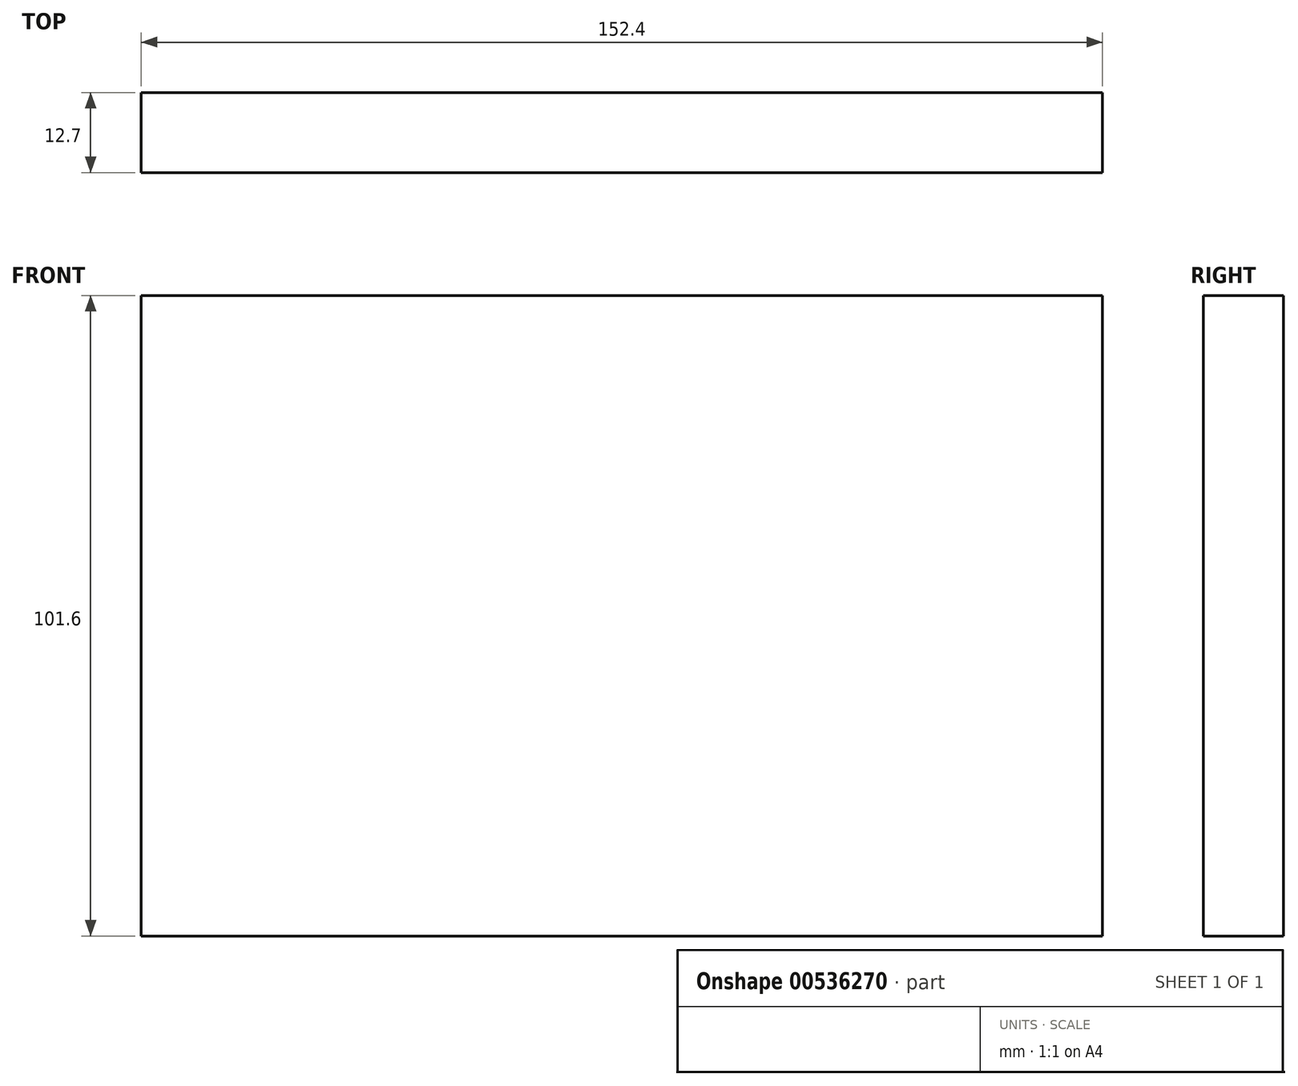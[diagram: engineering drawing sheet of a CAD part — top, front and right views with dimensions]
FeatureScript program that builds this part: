
annotation { "Feature Type Name" : "Feature", "Feature Type Description" : "" }
export const myFeature = defineFeature(function(context is Context, id is Id, definition is map)
    precondition{}
    {
        {
            var Q0;
            Q0=qCreatedBy(makeId("Front.planeOp"),FACE);
            var sketch = newSketch(context, id + "F0", { "sketchPlane" : qUnion([Q0])});
            skLineSegment(sketch, "E0.bottom", {"start": v(-76.2, 50.8) * mm, "end": v(76.2, 50.8) * mm});
            skLineSegment(sketch, "E0.top", {"start": v(-76.2, -50.8) * mm, "end": v(76.2, -50.8) * mm});
            skLineSegment(sketch, "E0.left", {"start": v(-76.2, 50.8) * mm, "end": v(-76.2, -50.8) * mm});
            skLineSegment(sketch, "E0.right", {"start": v(76.2, 50.8) * mm, "end": v(76.2, -50.8) * mm});
            skPoint(sketch, "E0.middle", {"position": v(0, 0) * mm});
            skSolve(sketch);
        }
        {
            var Q0;
            Q0 = qSketchRegion(id + "F0", true);
            extrude(context, id + "F1", {"entities" : qUnion([Q0]), "depth" : 12.7 * mm, "offsetDistance" : 25.4 * mm});
        }
    });
